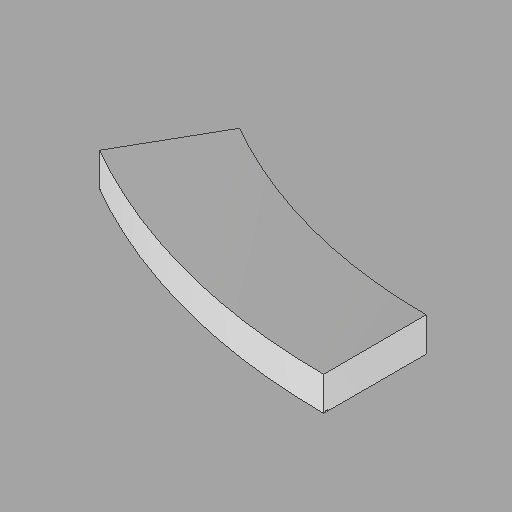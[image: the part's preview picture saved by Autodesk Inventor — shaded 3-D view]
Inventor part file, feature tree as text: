
AUTODESK INVENTOR PART (.ipt)
format: ipt  version: 2022.2 (Build 262287010, 287A)  size: 120,320 bytes
history: native  units: in
note: dims shown in document units (in); Inventor stores cm internally (conversion verified against a paired STEP export)
features: direct_edit x1, other x1, revolve x1
ambient origin geometry x8: Origin, YZ Plane, XZ Plane, XY Plane, X Axis, Y Axis, Z Axis, Center Point
bodies: Solid1 (feature_tree)
feature tree (3):
  direct_edit  "Direct Edit1"
  other  "Bottom cap (4) (2)"
  revolve  "Rotate1"  [1 undecoded]
note: 1 required parameter value undecoded (feature->parameter linkage not recoverable at this tier; creation-order binding heuristic only, values carry confidence <= 0.55)
